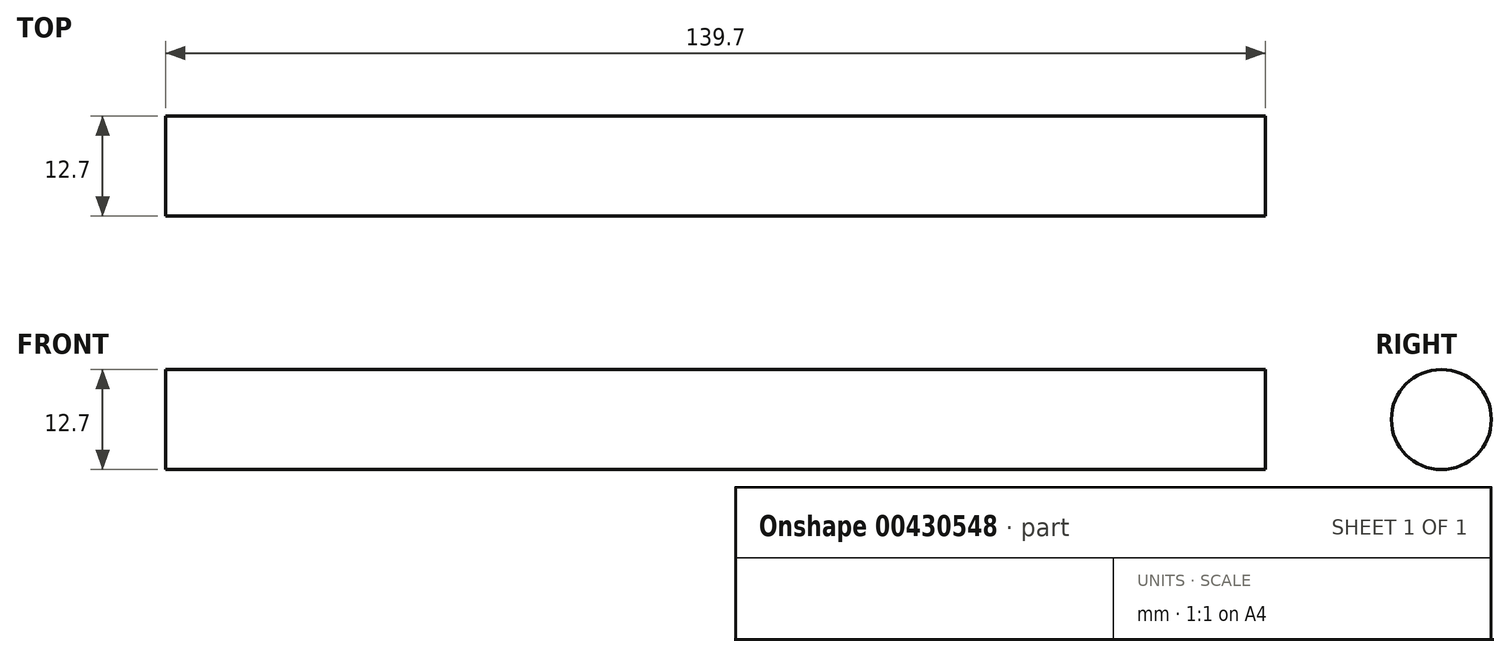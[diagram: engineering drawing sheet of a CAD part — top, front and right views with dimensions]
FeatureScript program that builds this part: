
annotation { "Feature Type Name" : "Feature", "Feature Type Description" : "" }
export const myFeature = defineFeature(function(context is Context, id is Id, definition is map)
    precondition{}
    {
        {
            var Q0;
            Q0=qCreatedBy(makeId("Right.planeOp"),FACE);
            var sketch = newSketch(context, id + "F0", { "sketchPlane" : qUnion([Q0])});
            skCircle(sketch, "E0", {"center": v(0, 0) * mm, "radius": 6.35 * mm});
            skSolve(sketch);
        }
        {
            var Q0;
            Q0=makeQuery(id+"F0.imprint","IMPRINT",FACE,{"disambiguationData":[TD([[makeQuery(id+"F0.imprint","IMPRINT",EDGE,{"derivedFrom":sQuery(id+"F0.wireOp",EDGE,"E0")}),1.0]])]});
            extrude(context, id + "F1", {"entities" : qUnion([Q0]), "depth" : 139.7 * mm});
        }
    });
